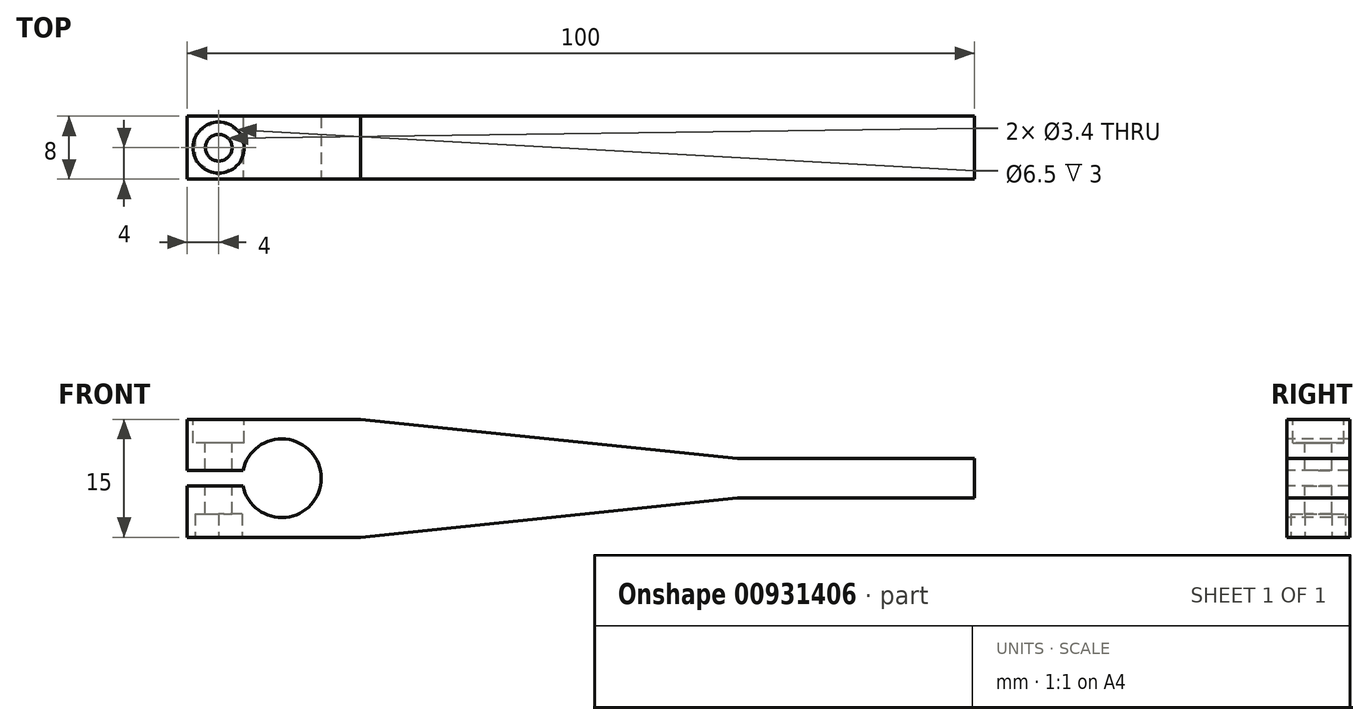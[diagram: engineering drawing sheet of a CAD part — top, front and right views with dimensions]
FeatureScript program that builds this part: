
annotation { "Feature Type Name" : "Feature", "Feature Type Description" : "" }
export const myFeature = defineFeature(function(context is Context, id is Id, definition is map)
    precondition{}
    {
        {
            var Q0;
            Q0=qCreatedBy(makeId("Top.planeOp"),FACE);
            var sketch = newSketch(context, id + "F0", { "sketchPlane" : qUnion([Q0])});
            skLineSegment(sketch, "E0.bottom", {"start": v(0, 0) * mm, "end": v(100, 0) * mm});
            skLineSegment(sketch, "E0.top", {"start": v(0, 8) * mm, "end": v(100, 8) * mm});
            skLineSegment(sketch, "E0.left", {"start": v(0, 0) * mm, "end": v(0, 8) * mm});
            skLineSegment(sketch, "E0.right", {"start": v(100, 0) * mm, "end": v(100, 8) * mm});
            skSolve(sketch);
        }
        {
            var Q0;
            Q0=makeQuery(id+"F0.imprint","IMPRINT",FACE,{"disambiguationData":[TD([[makeQuery(id+"F0.imprint","IMPRINT",EDGE,{"derivedFrom":sQuery(id+"F0.wireOp",EDGE,"E0.bottom")}),1.0]])]});
            extrude(context, id + "F1", {"entities" : qUnion([Q0]), "depth" : 15 * mm, "offsetDistance" : 25 * mm});
        }
        {
            var Q0;
            Q0=makeQuery(id+"F1.opExtrude","SWEPT_FACE",FACE,{"disambiguationData":[OSD([sQuery(id+"F0.wireOp",EDGE,"E0.bottom")])]});
            var sketch = newSketch(context, id + "F2", { "sketchPlane" : qUnion([Q0])});
            skArc(sketch, "E1", {"start": v(7.1, 6.5) * mm, "mid": v(17, 7.5) * mm, "end": v(7.1, 8.5) * mm});
            skLineSegment(sketch, "E2", {"start": v(100, 5) * mm, "end": v(70, 5) * mm});
            skLineSegment(sketch, "E3", {"start": v(70, 5) * mm, "end": v(22, 0) * mm});
            skLineSegment(sketch, "E4", {"start": v(22, 0) * mm, "end": v(100, 0) * mm});
            skLineSegment(sketch, "E5", {"start": v(100, 0) * mm, "end": v(100, 5) * mm});
            skLineSegment(sketch, "E6.bottom", {"start": v(0, 8.5) * mm, "end": v(7.1, 8.5) * mm});
            skLineSegment(sketch, "E6.top", {"start": v(0, 6.5) * mm, "end": v(7.1, 6.5) * mm});
            skLineSegment(sketch, "E6.left", {"start": v(0, 8.5) * mm, "end": v(0, 6.5) * mm});
            skLineSegment(sketch, "E7", {"start": v(100, 10) * mm, "end": v(70, 10) * mm});
            skLineSegment(sketch, "E8", {"start": v(70, 10) * mm, "end": v(22, 15) * mm});
            skLineSegment(sketch, "E9", {"start": v(22, 15) * mm, "end": v(100, 15) * mm});
            skLineSegment(sketch, "E10", {"start": v(100, 15) * mm, "end": v(100, 10) * mm});
            skSolve(sketch);
        }
        {
            var Q0;
            Q0=makeQuery(id+"F2.imprint","IMPRINT",FACE,{"disambiguationData":[TD([[makeQuery(id+"F2.imprint","IMPRINT",EDGE,{"derivedFrom":sQuery(id+"F2.wireOp",EDGE,"E2")}),1.0]])]});
            var Q1;
            Q1=makeQuery(id+"F2.imprint","IMPRINT",FACE,{"disambiguationData":[TD([[makeQuery(id+"F2.imprint","IMPRINT",EDGE,{"derivedFrom":sQuery(id+"F2.wireOp",EDGE,"E1")}),1.0]])]});
            var Q2;
            Q2=makeQuery(id+"F2.imprint","IMPRINT",FACE,{"disambiguationData":[TD([[makeQuery(id+"F2.imprint","IMPRINT",EDGE,{"derivedFrom":sQuery(id+"F2.wireOp",EDGE,"7crWbkx4-5Z7A-pysI-FyiN-YhfIFzFeSu20.bottom")}),1.0]])]});
            var Q3;
            Q3=makeQuery(id+"F2.imprint","IMPRINT",FACE,{"disambiguationData":[TD([[makeQuery(id+"F2.imprint","IMPRINT",EDGE,{"derivedFrom":sQuery(id+"F2.wireOp",EDGE,"mbcPeMDJ-fRm2-SM2C-fuVf-HlYfC1L1SrrV.bottom")}),-1.0]])]});
            var Q4;
            Q4=makeQuery(id+"F2.imprint","IMPRINT",FACE,{"disambiguationData":[TD([[makeQuery(id+"F2.imprint","IMPRINT",EDGE,{"derivedFrom":sQuery(id+"F2.wireOp",EDGE,"E7")}),-1.0]])]});
            extrude(context, id + "F3", {"entities" : qUnion([Q0, Q1, Q2, Q3, Q4]), "operationType" : NewBodyOperationType.REMOVE, "endBound" : BoundingType.UP_TO_NEXT, "oppositeDirection" : true, "depth" : 25 * mm, "offsetDistance" : 25 * mm});
        }
        {
            var Q0;
            Q0=makeQuery(id+"F1.opExtrude","CAP_FACE",FACE,{"disambiguationData":[OSD([sQuery(id+"F0.wireOp",EDGE,"E0.bottom"),sQuery(id+"F0.wireOp",EDGE,"E0.top"),sQuery(id+"F0.wireOp",EDGE,"E0.left"),sQuery(id+"F0.wireOp",EDGE,"E0.right")])],"isStart":true});
            var sketch = newSketch(context, id + "F4", { "sketchPlane" : qUnion([Q0])});
            skCircle(sketch, "E11.cCircle", {"center": v(4, -4) * mm, "radius": 3 * mm, "construction": true});
            skLineSegment(sketch, "E11.0", {"start": v(7, -5.73) * mm, "end": v(4, -7.46) * mm});
            skLineSegment(sketch, "E11.1", {"start": v(4, -7.46) * mm, "end": v(1, -5.73) * mm});
            skLineSegment(sketch, "E11.2", {"start": v(1, -5.73) * mm, "end": v(1, -2.27) * mm});
            skLineSegment(sketch, "E11.3", {"start": v(1, -2.27) * mm, "end": v(4, -0.54) * mm});
            skLineSegment(sketch, "E11.4", {"start": v(4, -0.54) * mm, "end": v(7, -2.27) * mm});
            skLineSegment(sketch, "E11.5", {"start": v(7, -2.27) * mm, "end": v(7, -5.73) * mm});
            skPoint(sketch, "E11.0.midPoint", {"position": v(5.5, -6.6) * mm});
            skSolve(sketch);
        }
        {
            var Q0;
            Q0=makeQuery(id+"F4.imprint","IMPRINT",FACE,{"disambiguationData":[TD([[makeQuery(id+"F4.imprint","IMPRINT",EDGE,{"derivedFrom":sQuery(id+"F4.wireOp",EDGE,"E11.0")}),-1.0]])]});
            extrude(context, id + "F5", {"entities" : qUnion([Q0]), "operationType" : NewBodyOperationType.REMOVE, "oppositeDirection" : true, "depth" : 3 * mm, "offsetDistance" : 25 * mm});
        }
        {
            var Q0;
            Q0=makeQuery(id+"F1.opExtrude","CAP_FACE",FACE,{"disambiguationData":[OSD([sQuery(id+"F0.wireOp",EDGE,"E0.bottom"),sQuery(id+"F0.wireOp",EDGE,"E0.top"),sQuery(id+"F0.wireOp",EDGE,"E0.left"),sQuery(id+"F0.wireOp",EDGE,"E0.right")])],"isStart":false});
            var sketch = newSketch(context, id + "F6", { "sketchPlane" : qUnion([Q0])});
            skPoint(sketch, "E12", {"position": v(4, 4) * mm});
            skSolve(sketch);
        }
        {
            var Q0;
            Q0=sQuery(id+"F6.wireOp",VERTEX,"E12");
            var Q1;
            Q1=makeQuery(id+"F1.opExtrude","SWEPT_BODY",BODY,{"disambiguationData":[OSD([sQuery(id+"F0.wireOp",EDGE,"E0.bottom"),sQuery(id+"F0.wireOp",EDGE,"E0.top"),sQuery(id+"F0.wireOp",EDGE,"E0.left"),sQuery(id+"F0.wireOp",EDGE,"E0.right")])]});
            hole(context, id + "F7", {"style" : HoleStyle.C_BORE, "endStyle" : HoleEndStyle.BLIND, "standardTappedOrClearance" : lookupTablePath({ "fit" : "Normal", "standard" : "ISO", "size" : "M3", "type" : "Clearance" }), "standardBlindInLast" : lookupTablePath({ "fit" : "Normal", "standard" : "ISO", "engagement" : "75%", "pitch" : "0.5 mm", "size" : "M3", "type" : "Clearance & tapped" }), "holeDiameter" : 3.4 * mm, "cBoreDiameter" : 6.5 * mm, "cBoreDepth" : 3 * mm, "majorDiameter" : 5 * mm, "holeDepth" : 15 * mm, "isTappedThrough" : true, "tappedDepth" : 12 * mm, "tapClearance" : 3, "locations" : qUnion([Q0]), "scope" : qUnion([Q1])});
        }
        {
            var Q0;
            Q0=makeQuery(id+"F3.boolean.opBoolean","COPY",EDGE,{"derivedFrom":makeQuery(id+"F3.opExtrude","SWEPT_EDGE",EDGE,{"disambiguationData":[OSD([sQuery(id+"F0.wireOp",EDGE,"E0.bottom"),sQuery(id+"F0.wireOp",EDGE,"E0.right"),sQuery(id+"F2.wireOp",EDGE,"E7"),sQuery(id+"F2.wireOp",EDGE,"E10")])]})});
            var Q1;
            Q1=makeQuery(id+"F3.boolean.opBoolean","COPY",EDGE,{"derivedFrom":makeQuery(id+"F3.opExtrude","SWEPT_EDGE",EDGE,{"disambiguationData":[OSD([sQuery(id+"F0.wireOp",EDGE,"E0.bottom"),sQuery(id+"F0.wireOp",EDGE,"E0.right"),sQuery(id+"F2.wireOp",EDGE,"E2"),sQuery(id+"F2.wireOp",EDGE,"E5")])]})});
            var Q2;
            Q2=makeQuery(id+"F3.boolean.opBoolean","COPY",EDGE,{"derivedFrom":makeQuery(id+"F3.opExtrude","SWEPT_EDGE",EDGE,{"disambiguationData":[OSD([sQuery(id+"F2.wireOp",EDGE,"E2"),sQuery(id+"F2.wireOp",EDGE,"E3")])]})});
            var Q3;
            Q3=makeQuery(id+"F3.boolean.opBoolean","COPY",EDGE,{"derivedFrom":makeQuery(id+"F3.opExtrude","SWEPT_EDGE",EDGE,{"disambiguationData":[OSD([sQuery(id+"F2.wireOp",EDGE,"E7"),sQuery(id+"F2.wireOp",EDGE,"E8")])]})});
            var Q4;
            Q4=makeQuery(id+"F3.boolean.opBoolean","COPY",EDGE,{"derivedFrom":makeQuery(id+"F3.opExtrude","SWEPT_EDGE",EDGE,{"disambiguationData":[OSD([sQuery(id+"F0.wireOp",EDGE,"E0.bottom"),sQuery(id+"F2.wireOp",EDGE,"E8"),sQuery(id+"F2.wireOp",EDGE,"E9")])]})});
            var Q5;
            Q5=makeQuery(id+"F3.boolean.opBoolean","COPY",EDGE,{"derivedFrom":makeQuery(id+"F3.opExtrude","SWEPT_EDGE",EDGE,{"disambiguationData":[OSD([sQuery(id+"F0.wireOp",EDGE,"E0.bottom"),sQuery(id+"F2.wireOp",EDGE,"E3"),sQuery(id+"F2.wireOp",EDGE,"E4")])]})});
            fillet(context, id + "F8", {"entities" : qUnion([Q0, Q1, Q2, Q3, Q4, Q5]), "tangentPropagation" : true, "radius" : 2 * mm, "defaultsChanged" : false, "vertexSettings" : [], "allowEdgeOverflow" : false});
        }
    });
